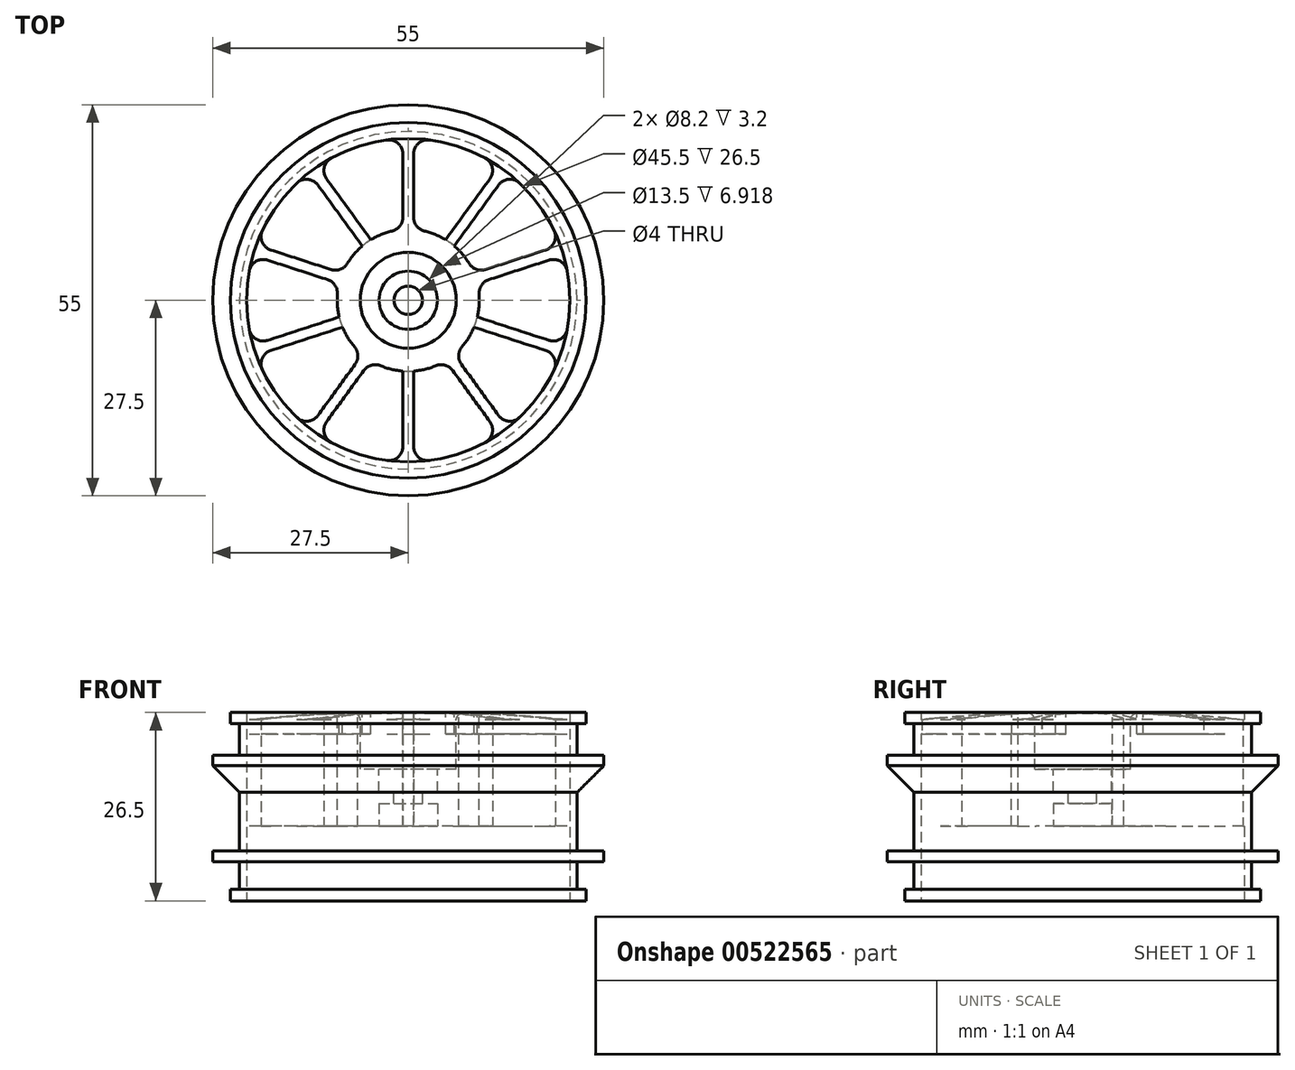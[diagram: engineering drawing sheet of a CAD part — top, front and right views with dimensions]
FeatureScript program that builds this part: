
annotation { "Feature Type Name" : "Feature", "Feature Type Description" : "" }
export const myFeature = defineFeature(function(context is Context, id is Id, definition is map)
    precondition{}
    {
        {
            var Q0;
            Q0=qCreatedBy(makeId("Top.planeOp"),FACE);
            var sketch = newSketch(context, id + "F0", { "sketchPlane" : qUnion([Q0])});
            skCircle(sketch, "E0", {"center": v(0, 0) * mm, "radius": 23.75 * mm});
            skCircle(sketch, "E1", {"center": v(0, 0) * mm, "radius": 22.75 * mm});
            skSolve(sketch);
        }
        {
            var Q0;
            Q0 = qSketchRegion(id + "F0", true);
            extrude(context, id + "F1", {"entities" : qUnion([Q0]), "depth" : 26.5 * mm, "offsetDistance" : 25 * mm});
        }
        {
            var Q0;
            Q0=qCreatedBy(makeId("Top.planeOp"),FACE);
            var sketch = newSketch(context, id + "F2", { "sketchPlane" : qUnion([Q0])});
            skCircle(sketch, "E2", {"center": v(0, 0) * mm, "radius": 25 * mm});
            skCircle(sketch, "E3", {"center": v(0, 0) * mm, "radius": 22.75 * mm});
            skSolve(sketch);
        }
        {
            var Q0;
            Q0 = qSketchRegion(id + "F2", true);
            extrude(context, id + "F3", {"entities" : qUnion([Q0]), "operationType" : NewBodyOperationType.ADD, "depth" : 1.6 * mm, "offsetDistance" : 25 * mm});
        }
        {
            var Q0;
            Q0=makeQuery(id+"F1.opExtrude","CAP_FACE",FACE,{"disambiguationData":[OSD([sQuery(id+"F0.wireOp",EDGE,"E0"),sQuery(id+"F0.wireOp",EDGE,"E1")])],"isStart":false});
            var sketch = newSketch(context, id + "F4", { "sketchPlane" : qUnion([Q0])});
            skCircle(sketch, "E4", {"center": v(0, 0) * mm, "radius": 22.75 * mm});
            skCircle(sketch, "E5", {"center": v(0, 0) * mm, "radius": 25 * mm});
            skSolve(sketch);
        }
        {
            var Q0;
            Q0 = qSketchRegion(id + "F4", true);
            extrude(context, id + "F5", {"entities" : qUnion([Q0]), "operationType" : NewBodyOperationType.ADD, "oppositeDirection" : true, "depth" : 1.6 * mm, "offsetDistance" : 25 * mm});
        }
        {
            var Q0;
            Q0=qCreatedBy(makeId("Top.planeOp"),FACE);
            cPlane(context, id + "F6", {"entities" : qUnion([Q0]), "cplaneType" : CPlaneType.OFFSET, "offset" : 5.5 * mm, "width" : 150 * mm, "height" : 150 * mm});
        }
        {
            var Q0;
            Q0=qCreatedBy(id+"F6.planeOp",FACE);
            var sketch = newSketch(context, id + "F7", { "sketchPlane" : qUnion([Q0])});
            skCircle(sketch, "E6", {"center": v(0, 0) * mm, "radius": 27.5 * mm});
            skCircle(sketch, "E7", {"center": v(0, 0) * mm, "radius": 22.75 * mm});
            skSolve(sketch);
        }
        {
            var Q0;
            Q0 = qSketchRegion(id + "F7", true);
            extrude(context, id + "F8", {"entities" : qUnion([Q0]), "operationType" : NewBodyOperationType.ADD, "depth" : 1.5 * mm, "offsetDistance" : 25 * mm});
        }
        {
            var Q0;
            Q0=qCreatedBy(makeId("Top.planeOp"),FACE);
            cPlane(context, id + "F9", {"entities" : qUnion([Q0]), "cplaneType" : CPlaneType.OFFSET, "offset" : 19 * mm, "width" : 150 * mm, "height" : 150 * mm});
        }
        {
            var Q0;
            Q0=qCreatedBy(id+"F9.planeOp",FACE);
            var sketch = newSketch(context, id + "F10", { "sketchPlane" : qUnion([Q0])});
            skCircle(sketch, "E8", {"center": v(0, 0) * mm, "radius": 27.5 * mm});
            skCircle(sketch, "E9", {"center": v(0, 0) * mm, "radius": 22.75 * mm});
            skSolve(sketch);
        }
        {
            var Q0;
            Q0 = qSketchRegion(id + "F10", true);
            extrude(context, id + "F11", {"entities" : qUnion([Q0]), "operationType" : NewBodyOperationType.ADD, "depth" : 1.5 * mm, "offsetDistance" : 25 * mm});
        }
        {
            var Q0;
            Q0=makeQuery(id+"F5.boolean.opBoolean","MERGE",FACE,{"derivedFrom":[makeQuery(id+"F1.opExtrude","CAP_FACE",FACE,{"disambiguationData":[OSD([sQuery(id+"F0.wireOp",EDGE,"E0"),sQuery(id+"F0.wireOp",EDGE,"E1")])],"isStart":false}),makeQuery(id+"F5.opExtrude","CAP_FACE",FACE,{"disambiguationData":[OSD([sQuery(id+"F4.wireOp",EDGE,"E4"),sQuery(id+"F4.wireOp",EDGE,"E5")])],"isStart":true})]});
            var sketch = newSketch(context, id + "F12", { "sketchPlane" : qUnion([Q0])});
            skLineSegment(sketch, "E10.top", {"start": v(-0.75, 23) * mm, "end": v(0.75, 23) * mm});
            skLineSegment(sketch, "E10.left", {"start": v(-0.75, 9.97) * mm, "end": v(-0.75, 23) * mm});
            skLineSegment(sketch, "E10.right", {"start": v(0.75, 9.97) * mm, "end": v(0.75, 23) * mm});
            skArc(sketch, "E11", {"start": v(-0.75, 9.97) * mm, "mid": v(-5.88, 8.1) * mm, "end": v(-9.25, 3.8) * mm});
            skLineSegment(sketch, "E12.1.0", {"start": v(9.25, 3.8) * mm, "end": v(21.64, 7.82) * mm});
            skLineSegment(sketch, "E12.1.1", {"start": v(9.72, 2.37) * mm, "end": v(22.1, 6.4) * mm});
            skLineSegment(sketch, "E12.1.2", {"start": v(21.64, 7.82) * mm, "end": v(22.1, 6.4) * mm});
            skLineSegment(sketch, "E12.2.0", {"start": v(6.47, -7.63) * mm, "end": v(14.13, -18.17) * mm});
            skLineSegment(sketch, "E12.2.1", {"start": v(5.25, -8.5) * mm, "end": v(12.91, -19.05) * mm});
            skLineSegment(sketch, "E12.2.2", {"start": v(14.13, -18.17) * mm, "end": v(12.91, -19.05) * mm});
            skLineSegment(sketch, "E12.3.0", {"start": v(-5.25, -8.5) * mm, "end": v(-12.91, -19.05) * mm});
            skLineSegment(sketch, "E12.3.1", {"start": v(-6.47, -7.63) * mm, "end": v(-14.13, -18.17) * mm});
            skLineSegment(sketch, "E12.3.2", {"start": v(-12.91, -19.05) * mm, "end": v(-14.13, -18.17) * mm});
            skLineSegment(sketch, "E12.4.0", {"start": v(-9.72, 2.37) * mm, "end": v(-22.1, 6.4) * mm});
            skLineSegment(sketch, "E12.4.1", {"start": v(-9.25, 3.8) * mm, "end": v(-21.64, 7.82) * mm});
            skLineSegment(sketch, "E12.4.2", {"start": v(-22.1, 6.4) * mm, "end": v(-21.64, 7.82) * mm});
            skLineSegment(sketch, "E12.anchor1", {"start": v(0, 0) * mm, "end": v(-0.75, 9.97) * mm, "construction": true});
            skLineSegment(sketch, "E12.anchor2", {"start": v(0, 0) * mm, "end": v(-9.72, 2.37) * mm, "construction": true});
            skArc(sketch, "E13.trimOffspring", {"start": v(-9.72, 2.37) * mm, "mid": v(-9.51, -3.1) * mm, "end": v(-6.47, -7.63) * mm});
            skArc(sketch, "E14.trimOffspring", {"start": v(-5.25, -8.5) * mm, "mid": v(0, -10) * mm, "end": v(5.25, -8.5) * mm});
            skArc(sketch, "E15.trimOffspring", {"start": v(6.47, -7.63) * mm, "mid": v(9.51, -3.1) * mm, "end": v(9.72, 2.37) * mm});
            skArc(sketch, "E16.trimOffspring", {"start": v(9.25, 3.8) * mm, "mid": v(5.88, 8.1) * mm, "end": v(0.75, 9.97) * mm});
            skSolve(sketch);
        }
        {
            var Q0;
            Q0 = qSketchRegion(id + "F12", true);
            extrude(context, id + "F13", {"entities" : qUnion([Q0]), "operationType" : NewBodyOperationType.ADD, "oppositeDirection" : true, "depth" : 16 * mm, "offsetDistance" : 25 * mm});
        }
        {
            var Q0;
            Q0=makeQuery(id+"F11.boolean.opBoolean","INTERSECT",EDGE,{"derivedFrom":[makeQuery(id+"F8.boolean.opBoolean","SPLIT",FACE,{"disambiguationData":[TD([makeQuery(id+"F5.opExtrude","CAP_FACE",FACE,{"disambiguationData":[OSD([sQuery(id+"F4.wireOp",EDGE,"E4"),sQuery(id+"F4.wireOp",EDGE,"E5")])],"isStart":false})])],"derivedFrom":makeQuery(id+"F1.opExtrude","SWEPT_FACE",FACE,{"disambiguationData":[OSD([sQuery(id+"F0.wireOp",EDGE,"E0")])]})}),makeQuery(id+"F11.opExtrude","CAP_FACE",FACE,{"disambiguationData":[OSD([sQuery(id+"F10.wireOp",EDGE,"E8"),sQuery(id+"F10.wireOp",EDGE,"E9")])],"isStart":true})]});
            chamfer(context, id + "F14", {"entities" : qUnion([Q0]), "width" : 3.75 * mm, "tangentPropagation" : true});
        }
        {
            var Q0;
            Q0=makeQuery(id+"F13.boolean.opBoolean","MERGE",FACE,{"derivedFrom":[makeQuery(id+"F5.boolean.opBoolean","MERGE",FACE,{"derivedFrom":[makeQuery(id+"F1.opExtrude","CAP_FACE",FACE,{"disambiguationData":[OSD([sQuery(id+"F0.wireOp",EDGE,"E0"),sQuery(id+"F0.wireOp",EDGE,"E1")])],"isStart":false}),makeQuery(id+"F5.opExtrude","CAP_FACE",FACE,{"disambiguationData":[OSD([sQuery(id+"F4.wireOp",EDGE,"E4"),sQuery(id+"F4.wireOp",EDGE,"E5")])],"isStart":true})]}),makeQuery(id+"F13.opExtrude","CAP_FACE",FACE,{"disambiguationData":[OSD([sQuery(id+"F12.wireOp",EDGE,"E10.top"),sQuery(id+"F12.wireOp",EDGE,"E10.left"),sQuery(id+"F12.wireOp",EDGE,"E10.right"),sQuery(id+"F12.wireOp",EDGE,"E11"),sQuery(id+"F12.wireOp",EDGE,"E12.1.0"),sQuery(id+"F12.wireOp",EDGE,"E12.1.1"),sQuery(id+"F12.wireOp",EDGE,"E12.1.2"),sQuery(id+"F12.wireOp",EDGE,"E12.2.0"),sQuery(id+"F12.wireOp",EDGE,"E12.2.1"),sQuery(id+"F12.wireOp",EDGE,"E12.2.2"),sQuery(id+"F12.wireOp",EDGE,"E12.3.0"),sQuery(id+"F12.wireOp",EDGE,"E12.3.1"),sQuery(id+"F12.wireOp",EDGE,"E12.3.2"),sQuery(id+"F12.wireOp",EDGE,"E12.4.0"),sQuery(id+"F12.wireOp",EDGE,"E12.4.1"),sQuery(id+"F12.wireOp",EDGE,"E12.4.2"),sQuery(id+"F12.wireOp",EDGE,"E13.trimOffspring"),sQuery(id+"F12.wireOp",EDGE,"E14.trimOffspring"),sQuery(id+"F12.wireOp",EDGE,"E15.trimOffspring"),sQuery(id+"F12.wireOp",EDGE,"E16.trimOffspring")])],"isStart":true})]});
            var sketch = newSketch(context, id + "F15", { "sketchPlane" : qUnion([Q0])});
            skArc(sketch, "E17", {"start": v(-0.75, 9.97) * mm, "mid": v(-3.1, 9.51) * mm, "end": v(-5.25, 8.5) * mm});
            skLineSegment(sketch, "E18", {"start": v(-0.75, 9.97) * mm, "end": v(-0.75, 22.97) * mm});
            skLineSegment(sketch, "E19", {"start": v(0.75, 22.97) * mm, "end": v(0.75, 9.97) * mm});
            skLineSegment(sketch, "E20.1.0", {"start": v(-6.47, 7.63) * mm, "end": v(-14.11, 18.14) * mm});
            skLineSegment(sketch, "E20.1.1", {"start": v(-12.9, 19.02) * mm, "end": v(-5.25, 8.5) * mm});
            skLineSegment(sketch, "E20.2.0", {"start": v(-9.72, 2.37) * mm, "end": v(-22.08, 6.38) * mm});
            skLineSegment(sketch, "E20.2.1", {"start": v(-21.62, 7.8) * mm, "end": v(-9.25, 3.8) * mm});
            skLineSegment(sketch, "E20.3.0", {"start": v(-9.25, -3.8) * mm, "end": v(-21.62, -7.81) * mm});
            skLineSegment(sketch, "E20.3.1", {"start": v(-22.08, -6.39) * mm, "end": v(-9.72, -2.37) * mm});
            skLineSegment(sketch, "E20.4.0", {"start": v(-5.25, -8.5) * mm, "end": v(-12.9, -19.03) * mm});
            skLineSegment(sketch, "E20.4.1", {"start": v(-14.1, -18.15) * mm, "end": v(-6.47, -7.63) * mm});
            skLineSegment(sketch, "E20.5.0", {"start": v(0.75, -9.97) * mm, "end": v(0.75, -22.97) * mm});
            skLineSegment(sketch, "E20.5.1", {"start": v(-0.75, -22.97) * mm, "end": v(-0.75, -9.97) * mm});
            skLineSegment(sketch, "E20.6.0", {"start": v(6.47, -7.63) * mm, "end": v(14.11, -18.14) * mm});
            skLineSegment(sketch, "E20.6.1", {"start": v(12.9, -19.02) * mm, "end": v(5.25, -8.5) * mm});
            skLineSegment(sketch, "E20.7.0", {"start": v(9.72, -2.37) * mm, "end": v(22.08, -6.38) * mm});
            skLineSegment(sketch, "E20.7.1", {"start": v(21.62, -7.8) * mm, "end": v(9.25, -3.8) * mm});
            skLineSegment(sketch, "E20.8.0", {"start": v(9.25, 3.8) * mm, "end": v(21.62, 7.81) * mm});
            skLineSegment(sketch, "E20.8.1", {"start": v(22.08, 6.39) * mm, "end": v(9.72, 2.37) * mm});
            skLineSegment(sketch, "E20.9.0", {"start": v(5.25, 8.5) * mm, "end": v(12.9, 19.03) * mm});
            skLineSegment(sketch, "E20.9.1", {"start": v(14.1, 18.15) * mm, "end": v(6.47, 7.63) * mm});
            skArc(sketch, "E21.trimOffspring", {"start": v(-9.72, 2.37) * mm, "mid": v(-10, 0) * mm, "end": v(-9.72, -2.37) * mm});
            skArc(sketch, "E22.trimOffspring", {"start": v(-5.25, -8.5) * mm, "mid": v(-3.1, -9.51) * mm, "end": v(-0.75, -9.97) * mm});
            skArc(sketch, "E23.trimOffspring", {"start": v(9.72, -2.37) * mm, "mid": v(10, 0) * mm, "end": v(9.72, 2.37) * mm});
            skArc(sketch, "E24.trimOffspring", {"start": v(6.47, -7.63) * mm, "mid": v(8.1, -5.88) * mm, "end": v(9.25, -3.8) * mm});
            skArc(sketch, "E25.trimOffspring", {"start": v(0.75, -9.97) * mm, "mid": v(3.1, -9.51) * mm, "end": v(5.25, -8.5) * mm});
            skArc(sketch, "E26.trimOffspring", {"start": v(-9.25, -3.8) * mm, "mid": v(-8.1, -5.88) * mm, "end": v(-6.47, -7.63) * mm});
            skArc(sketch, "E27.trimOffspring", {"start": v(-6.47, 7.63) * mm, "mid": v(-8.1, 5.88) * mm, "end": v(-9.25, 3.8) * mm});
            skArc(sketch, "E28.trimOffspring", {"start": v(5.25, 8.5) * mm, "mid": v(3.1, 9.51) * mm, "end": v(0.75, 9.97) * mm});
            skArc(sketch, "E29.trimOffspring", {"start": v(9.25, 3.8) * mm, "mid": v(8.1, 5.88) * mm, "end": v(6.47, 7.63) * mm});
            skLineSegment(sketch, "E30", {"start": v(-12.9, 19.02) * mm, "end": v(-14.11, 18.14) * mm});
            skLineSegment(sketch, "E31", {"start": v(-21.62, 7.8) * mm, "end": v(-22.08, 6.38) * mm});
            skLineSegment(sketch, "E32", {"start": v(-22.08, -6.39) * mm, "end": v(-21.62, -7.81) * mm});
            skLineSegment(sketch, "E33", {"start": v(-14.1, -18.15) * mm, "end": v(-12.9, -19.03) * mm});
            skLineSegment(sketch, "E34", {"start": v(-0.75, -22.97) * mm, "end": v(0.75, -22.97) * mm});
            skLineSegment(sketch, "E35", {"start": v(14.11, -18.14) * mm, "end": v(12.9, -19.02) * mm});
            skLineSegment(sketch, "E36", {"start": v(22.08, -6.38) * mm, "end": v(21.62, -7.8) * mm});
            skLineSegment(sketch, "E37", {"start": v(21.62, 7.81) * mm, "end": v(22.08, 6.39) * mm});
            skLineSegment(sketch, "E38", {"start": v(12.9, 19.03) * mm, "end": v(14.1, 18.15) * mm});
            skLineSegment(sketch, "E39", {"start": v(-0.75, 22.97) * mm, "end": v(0.75, 22.97) * mm});
            skSolve(sketch);
        }
        {
            var Q0;
            Q0 = qSketchRegion(id + "F15", true);
            extrude(context, id + "F16", {"entities" : qUnion([Q0]), "operationType" : NewBodyOperationType.ADD, "oppositeDirection" : true, "depth" : 3 * mm, "offsetDistance" : 25 * mm});
        }
        {
            var Q0;
            Q0=makeQuery(id+"F16.boolean.opBoolean","INTERSECT",EDGE,{"derivedFrom":[makeQuery(id+"F1.opExtrude","SWEPT_FACE",FACE,{"disambiguationData":[OSD([sQuery(id+"F0.wireOp",EDGE,"E1")])]}),makeQuery(id+"F16.opExtrude","SWEPT_FACE",FACE,{"disambiguationData":[OSD([sQuery(id+"F15.wireOp",EDGE,"E20.1.0")])]})]});
            var Q1;
            Q1=makeQuery(id+"F16.boolean.opBoolean","INTERSECT",EDGE,{"derivedFrom":[makeQuery(id+"F1.opExtrude","SWEPT_FACE",FACE,{"disambiguationData":[OSD([sQuery(id+"F0.wireOp",EDGE,"E1")])]}),makeQuery(id+"F16.opExtrude","SWEPT_FACE",FACE,{"disambiguationData":[OSD([sQuery(id+"F15.wireOp",EDGE,"E20.1.1")])]})]});
            var Q2;
            Q2=makeQuery(id+"F16.opExtrude","SWEPT_EDGE",EDGE,{"disambiguationData":[OSD([sQuery(id+"F12.wireOp",EDGE,"E11"),sQuery(id+"F15.wireOp",EDGE,"E20.1.0"),sQuery(id+"F15.wireOp",EDGE,"E27.trimOffspring")])]});
            var Q3;
            Q3=makeQuery(id+"F13.boolean.opBoolean","INTERSECT",EDGE,{"derivedFrom":[makeQuery(id+"F1.opExtrude","SWEPT_FACE",FACE,{"disambiguationData":[OSD([sQuery(id+"F0.wireOp",EDGE,"E1")])]}),makeQuery(id+"F13.opExtrude","SWEPT_FACE",FACE,{"disambiguationData":[OSD([sQuery(id+"F12.wireOp",EDGE,"E12.4.1")])]})]});
            var Q4;
            Q4=makeQuery(id+"F13.opExtrude","SWEPT_EDGE",EDGE,{"disambiguationData":[OSD([sQuery(id+"F12.wireOp",EDGE,"E11"),sQuery(id+"F12.wireOp",EDGE,"E12.4.1")])]});
            var Q5;
            Q5=makeQuery(id+"F13.opExtrude","SWEPT_EDGE",EDGE,{"disambiguationData":[OSD([sQuery(id+"F12.wireOp",EDGE,"E10.left"),sQuery(id+"F12.wireOp",EDGE,"E11")])]});
            var Q6;
            Q6=makeQuery(id+"F13.boolean.opBoolean","INTERSECT",EDGE,{"derivedFrom":[makeQuery(id+"F1.opExtrude","SWEPT_FACE",FACE,{"disambiguationData":[OSD([sQuery(id+"F0.wireOp",EDGE,"E1")])]}),makeQuery(id+"F13.opExtrude","SWEPT_FACE",FACE,{"disambiguationData":[OSD([sQuery(id+"F12.wireOp",EDGE,"E10.left")])]})]});
            var Q7;
            Q7=makeQuery(id+"F16.opExtrude","SWEPT_EDGE",EDGE,{"disambiguationData":[OSD([sQuery(id+"F12.wireOp",EDGE,"E11"),sQuery(id+"F15.wireOp",EDGE,"E17"),sQuery(id+"F15.wireOp",EDGE,"E20.1.1")])]});
            var Q8;
            Q8=makeQuery(id+"F16.opExtrude","SWEPT_EDGE",EDGE,{"disambiguationData":[OSD([sQuery(id+"F12.wireOp",EDGE,"E16.trimOffspring"),sQuery(id+"F15.wireOp",EDGE,"E20.9.0"),sQuery(id+"F15.wireOp",EDGE,"E28.trimOffspring")])]});
            var Q9;
            Q9=makeQuery(id+"F13.opExtrude","SWEPT_EDGE",EDGE,{"disambiguationData":[OSD([sQuery(id+"F12.wireOp",EDGE,"E10.right"),sQuery(id+"F12.wireOp",EDGE,"E16.trimOffspring")])]});
            var Q10;
            Q10=makeQuery(id+"F13.opExtrude","SWEPT_EDGE",EDGE,{"disambiguationData":[OSD([sQuery(id+"F12.wireOp",EDGE,"E12.1.0"),sQuery(id+"F12.wireOp",EDGE,"E16.trimOffspring")])]});
            var Q11;
            Q11=makeQuery(id+"F13.boolean.opBoolean","INTERSECT",EDGE,{"derivedFrom":[makeQuery(id+"F1.opExtrude","SWEPT_FACE",FACE,{"disambiguationData":[OSD([sQuery(id+"F0.wireOp",EDGE,"E1")])]}),makeQuery(id+"F13.opExtrude","SWEPT_FACE",FACE,{"disambiguationData":[OSD([sQuery(id+"F12.wireOp",EDGE,"E10.right")])]})]});
            var Q12;
            Q12=makeQuery(id+"F16.boolean.opBoolean","INTERSECT",EDGE,{"derivedFrom":[makeQuery(id+"F1.opExtrude","SWEPT_FACE",FACE,{"disambiguationData":[OSD([sQuery(id+"F0.wireOp",EDGE,"E1")])]}),makeQuery(id+"F16.opExtrude","SWEPT_FACE",FACE,{"disambiguationData":[OSD([sQuery(id+"F15.wireOp",EDGE,"E20.9.0")])]})]});
            var Q13;
            Q13=makeQuery(id+"F13.boolean.opBoolean","INTERSECT",EDGE,{"derivedFrom":[makeQuery(id+"F1.opExtrude","SWEPT_FACE",FACE,{"disambiguationData":[OSD([sQuery(id+"F0.wireOp",EDGE,"E1")])]}),makeQuery(id+"F13.opExtrude","SWEPT_FACE",FACE,{"disambiguationData":[OSD([sQuery(id+"F12.wireOp",EDGE,"E12.1.0")])]})]});
            var Q14;
            Q14=makeQuery(id+"F13.boolean.opBoolean","INTERSECT",EDGE,{"derivedFrom":[makeQuery(id+"F1.opExtrude","SWEPT_FACE",FACE,{"disambiguationData":[OSD([sQuery(id+"F0.wireOp",EDGE,"E1")])]}),makeQuery(id+"F13.opExtrude","SWEPT_FACE",FACE,{"disambiguationData":[OSD([sQuery(id+"F12.wireOp",EDGE,"E12.1.1")])]})]});
            var Q15;
            Q15=makeQuery(id+"F13.opExtrude","SWEPT_EDGE",EDGE,{"disambiguationData":[OSD([sQuery(id+"F12.wireOp",EDGE,"E12.1.1"),sQuery(id+"F12.wireOp",EDGE,"E15.trimOffspring")])]});
            var Q16;
            Q16=makeQuery(id+"F16.opExtrude","SWEPT_EDGE",EDGE,{"disambiguationData":[OSD([sQuery(id+"F12.wireOp",EDGE,"E15.trimOffspring"),sQuery(id+"F15.wireOp",EDGE,"E20.7.1"),sQuery(id+"F15.wireOp",EDGE,"E24.trimOffspring")])]});
            var Q17;
            Q17=makeQuery(id+"F13.opExtrude","SWEPT_EDGE",EDGE,{"disambiguationData":[OSD([sQuery(id+"F12.wireOp",EDGE,"E12.2.0"),sQuery(id+"F12.wireOp",EDGE,"E15.trimOffspring")])]});
            var Q18;
            Q18=makeQuery(id+"F16.opExtrude","SWEPT_EDGE",EDGE,{"disambiguationData":[OSD([sQuery(id+"F12.wireOp",EDGE,"E14.trimOffspring"),sQuery(id+"F15.wireOp",EDGE,"E20.5.0"),sQuery(id+"F15.wireOp",EDGE,"E25.trimOffspring")])]});
            var Q19;
            Q19=makeQuery(id+"F13.boolean.opBoolean","INTERSECT",EDGE,{"derivedFrom":[makeQuery(id+"F1.opExtrude","SWEPT_FACE",FACE,{"disambiguationData":[OSD([sQuery(id+"F0.wireOp",EDGE,"E1")])]}),makeQuery(id+"F13.opExtrude","SWEPT_FACE",FACE,{"disambiguationData":[OSD([sQuery(id+"F12.wireOp",EDGE,"E12.3.0")])]})]});
            var Q20;
            Q20=makeQuery(id+"F16.boolean.opBoolean","INTERSECT",EDGE,{"derivedFrom":[makeQuery(id+"F1.opExtrude","SWEPT_FACE",FACE,{"disambiguationData":[OSD([sQuery(id+"F0.wireOp",EDGE,"E1")])]}),makeQuery(id+"F16.opExtrude","SWEPT_FACE",FACE,{"disambiguationData":[OSD([sQuery(id+"F15.wireOp",EDGE,"E20.3.0")])]})]});
            var Q21;
            Q21=makeQuery(id+"F13.boolean.opBoolean","INTERSECT",EDGE,{"derivedFrom":[makeQuery(id+"F1.opExtrude","SWEPT_FACE",FACE,{"disambiguationData":[OSD([sQuery(id+"F0.wireOp",EDGE,"E1")])]}),makeQuery(id+"F13.opExtrude","SWEPT_FACE",FACE,{"disambiguationData":[OSD([sQuery(id+"F12.wireOp",EDGE,"E12.4.0")])]})]});
            var Q22;
            Q22=makeQuery(id+"F16.boolean.opBoolean","INTERSECT",EDGE,{"derivedFrom":[makeQuery(id+"F1.opExtrude","SWEPT_FACE",FACE,{"disambiguationData":[OSD([sQuery(id+"F0.wireOp",EDGE,"E1")])]}),makeQuery(id+"F16.opExtrude","SWEPT_FACE",FACE,{"disambiguationData":[OSD([sQuery(id+"F15.wireOp",EDGE,"E20.9.1")])]})]});
            var Q23;
            Q23=makeQuery(id+"F16.boolean.opBoolean","INTERSECT",EDGE,{"derivedFrom":[makeQuery(id+"F1.opExtrude","SWEPT_FACE",FACE,{"disambiguationData":[OSD([sQuery(id+"F0.wireOp",EDGE,"E1")])]}),makeQuery(id+"F16.opExtrude","SWEPT_FACE",FACE,{"disambiguationData":[OSD([sQuery(id+"F15.wireOp",EDGE,"E20.7.1")])]})]});
            var Q24;
            Q24=makeQuery(id+"F16.opExtrude","SWEPT_EDGE",EDGE,{"disambiguationData":[OSD([sQuery(id+"F12.wireOp",EDGE,"E13.trimOffspring"),sQuery(id+"F15.wireOp",EDGE,"E20.3.0"),sQuery(id+"F15.wireOp",EDGE,"E26.trimOffspring")])]});
            var Q25;
            Q25=makeQuery(id+"F13.opExtrude","SWEPT_EDGE",EDGE,{"disambiguationData":[OSD([sQuery(id+"F12.wireOp",EDGE,"E12.4.0"),sQuery(id+"F12.wireOp",EDGE,"E13.trimOffspring")])]});
            var Q26;
            Q26=makeQuery(id+"F13.opExtrude","SWEPT_EDGE",EDGE,{"disambiguationData":[OSD([sQuery(id+"F12.wireOp",EDGE,"E12.3.1"),sQuery(id+"F12.wireOp",EDGE,"E13.trimOffspring")])]});
            var Q27;
            Q27=makeQuery(id+"F16.opExtrude","SWEPT_EDGE",EDGE,{"disambiguationData":[OSD([sQuery(id+"F12.wireOp",EDGE,"E14.trimOffspring"),sQuery(id+"F15.wireOp",EDGE,"E20.5.1"),sQuery(id+"F15.wireOp",EDGE,"E22.trimOffspring")])]});
            var Q28;
            Q28=makeQuery(id+"F13.opExtrude","SWEPT_EDGE",EDGE,{"disambiguationData":[OSD([sQuery(id+"F12.wireOp",EDGE,"E12.2.1"),sQuery(id+"F12.wireOp",EDGE,"E14.trimOffspring")])]});
            var Q29;
            Q29=makeQuery(id+"F13.boolean.opBoolean","INTERSECT",EDGE,{"derivedFrom":[makeQuery(id+"F1.opExtrude","SWEPT_FACE",FACE,{"disambiguationData":[OSD([sQuery(id+"F0.wireOp",EDGE,"E1")])]}),makeQuery(id+"F13.opExtrude","SWEPT_FACE",FACE,{"disambiguationData":[OSD([sQuery(id+"F12.wireOp",EDGE,"E12.2.1")])]})]});
            var Q30;
            Q30=makeQuery(id+"F13.boolean.opBoolean","INTERSECT",EDGE,{"derivedFrom":[makeQuery(id+"F1.opExtrude","SWEPT_FACE",FACE,{"disambiguationData":[OSD([sQuery(id+"F0.wireOp",EDGE,"E1")])]}),makeQuery(id+"F13.opExtrude","SWEPT_FACE",FACE,{"disambiguationData":[OSD([sQuery(id+"F12.wireOp",EDGE,"E12.2.0")])]})]});
            var Q31;
            Q31=makeQuery(id+"F16.boolean.opBoolean","INTERSECT",EDGE,{"derivedFrom":[makeQuery(id+"F1.opExtrude","SWEPT_FACE",FACE,{"disambiguationData":[OSD([sQuery(id+"F0.wireOp",EDGE,"E1")])]}),makeQuery(id+"F16.opExtrude","SWEPT_FACE",FACE,{"disambiguationData":[OSD([sQuery(id+"F15.wireOp",EDGE,"E20.5.0")])]})]});
            var Q32;
            Q32=makeQuery(id+"F16.boolean.opBoolean","INTERSECT",EDGE,{"derivedFrom":[makeQuery(id+"F1.opExtrude","SWEPT_FACE",FACE,{"disambiguationData":[OSD([sQuery(id+"F0.wireOp",EDGE,"E1")])]}),makeQuery(id+"F16.opExtrude","SWEPT_FACE",FACE,{"disambiguationData":[OSD([sQuery(id+"F15.wireOp",EDGE,"E20.5.1")])]})]});
            var Q33;
            Q33=makeQuery(id+"F13.boolean.opBoolean","INTERSECT",EDGE,{"derivedFrom":[makeQuery(id+"F1.opExtrude","SWEPT_FACE",FACE,{"disambiguationData":[OSD([sQuery(id+"F0.wireOp",EDGE,"E1")])]}),makeQuery(id+"F13.opExtrude","SWEPT_FACE",FACE,{"disambiguationData":[OSD([sQuery(id+"F12.wireOp",EDGE,"E12.3.1")])]})]});
            var Q34;
            Q34=makeQuery(id+"F16.boolean.opBoolean","INTERSECT",EDGE,{"derivedFrom":[makeQuery(id+"F1.opExtrude","SWEPT_FACE",FACE,{"disambiguationData":[OSD([sQuery(id+"F0.wireOp",EDGE,"E1")])]}),makeQuery(id+"F16.opExtrude","SWEPT_FACE",FACE,{"disambiguationData":[OSD([sQuery(id+"F15.wireOp",EDGE,"E20.3.1")])]})]});
            var Q35;
            Q35=makeQuery(id+"F13.opExtrude","SWEPT_EDGE",EDGE,{"disambiguationData":[OSD([sQuery(id+"F12.wireOp",EDGE,"E12.3.0"),sQuery(id+"F12.wireOp",EDGE,"E14.trimOffspring")])]});
            var Q36;
            Q36=makeQuery(id+"F16.opExtrude","SWEPT_EDGE",EDGE,{"disambiguationData":[OSD([sQuery(id+"F12.wireOp",EDGE,"E16.trimOffspring"),sQuery(id+"F15.wireOp",EDGE,"E20.9.1"),sQuery(id+"F15.wireOp",EDGE,"E29.trimOffspring")])]});
            var Q37;
            Q37=makeQuery(id+"F16.opExtrude","SWEPT_EDGE",EDGE,{"disambiguationData":[OSD([sQuery(id+"F12.wireOp",EDGE,"E15.trimOffspring"),sQuery(id+"F15.wireOp",EDGE,"E20.7.0"),sQuery(id+"F15.wireOp",EDGE,"E23.trimOffspring")])]});
            var Q38;
            Q38=makeQuery(id+"F16.boolean.opBoolean","INTERSECT",EDGE,{"derivedFrom":[makeQuery(id+"F1.opExtrude","SWEPT_FACE",FACE,{"disambiguationData":[OSD([sQuery(id+"F0.wireOp",EDGE,"E1")])]}),makeQuery(id+"F16.opExtrude","SWEPT_FACE",FACE,{"disambiguationData":[OSD([sQuery(id+"F15.wireOp",EDGE,"E20.7.0")])]})]});
            var Q39;
            Q39=makeQuery(id+"F16.opExtrude","SWEPT_EDGE",EDGE,{"disambiguationData":[OSD([sQuery(id+"F12.wireOp",EDGE,"E13.trimOffspring"),sQuery(id+"F15.wireOp",EDGE,"E20.3.1"),sQuery(id+"F15.wireOp",EDGE,"E21.trimOffspring")])]});
            fillet(context, id + "F17", {"entities" : qUnion([Q0, Q1, Q2, Q3, Q4, Q5, Q6, Q7, Q8, Q9, Q10, Q11, Q12, Q13, Q14, Q15, Q16, Q17, Q18, Q19, Q20, Q21, Q22, Q23, Q24, Q25, Q26, Q27, Q28, Q29, Q30, Q31, Q32, Q33, Q34, Q35, Q36, Q37, Q38, Q39]), "radius" : 2 * mm, "tangentPropagation" : true, "allowEdgeOverflow" : false});
        }
        {
            var Q0;
            Q0=qCreatedBy(makeId("Front.planeOp"),FACE);
            var sketch = newSketch(context, id + "F18", { "sketchPlane" : qUnion([Q0])});
            skLineSegment(sketch, "E40", {"start": v(0, 27.5) * mm, "end": v(22.75, 27.5) * mm});
            skLineSegment(sketch, "E41", {"start": v(22.75, 27.5) * mm, "end": v(22.75, 25.5) * mm});
            skFitSpline(sketch, "E42", {"points": [v(22.75, 25.5) * mm, v(12.74, 26.28) * mm, v(0, 26.5) * mm], "startDerivative": vector(-15.68, 1.36) * mm, "endDerivative": vector(-21.9, 0.46) * mm});
            skLineSegment(sketch, "E43", {"start": v(0, 26.5) * mm, "end": v(0, 27.5) * mm});
            skSolve(sketch);
        }
        {
            var Q0;
            Q0 = qSketchRegion(id + "F18", true);
            var Q1;
            Q1=sQuery(id+"F18.wireOp",EDGE,"E43");
            revolve(context, id + "F19", {"operationType" : NewBodyOperationType.REMOVE, "entities" : qUnion([Q0]), "axis" : qUnion([Q1]), "revolveType" : RevolveType.FULL});
        }
        {
            var Q0;
            Q0=makeQuery(id+"F16.boolean.opBoolean","MERGE",FACE,{"derivedFrom":[makeQuery(id+"F13.boolean.opBoolean","MERGE",FACE,{"derivedFrom":[makeQuery(id+"F5.boolean.opBoolean","MERGE",FACE,{"derivedFrom":[makeQuery(id+"F1.opExtrude","CAP_FACE",FACE,{"disambiguationData":[OSD([sQuery(id+"F0.wireOp",EDGE,"E0"),sQuery(id+"F0.wireOp",EDGE,"E1")])],"isStart":false}),makeQuery(id+"F5.opExtrude","CAP_FACE",FACE,{"disambiguationData":[OSD([sQuery(id+"F4.wireOp",EDGE,"E4"),sQuery(id+"F4.wireOp",EDGE,"E5")])],"isStart":true})]}),makeQuery(id+"F13.opExtrude","CAP_FACE",FACE,{"disambiguationData":[OSD([sQuery(id+"F12.wireOp",EDGE,"E10.top"),sQuery(id+"F12.wireOp",EDGE,"E10.left"),sQuery(id+"F12.wireOp",EDGE,"E10.right"),sQuery(id+"F12.wireOp",EDGE,"E11"),sQuery(id+"F12.wireOp",EDGE,"E12.1.0"),sQuery(id+"F12.wireOp",EDGE,"E12.1.1"),sQuery(id+"F12.wireOp",EDGE,"E12.1.2"),sQuery(id+"F12.wireOp",EDGE,"E12.2.0"),sQuery(id+"F12.wireOp",EDGE,"E12.2.1"),sQuery(id+"F12.wireOp",EDGE,"E12.2.2"),sQuery(id+"F12.wireOp",EDGE,"E12.3.0"),sQuery(id+"F12.wireOp",EDGE,"E12.3.1"),sQuery(id+"F12.wireOp",EDGE,"E12.3.2"),sQuery(id+"F12.wireOp",EDGE,"E12.4.0"),sQuery(id+"F12.wireOp",EDGE,"E12.4.1"),sQuery(id+"F12.wireOp",EDGE,"E12.4.2"),sQuery(id+"F12.wireOp",EDGE,"E13.trimOffspring"),sQuery(id+"F12.wireOp",EDGE,"E14.trimOffspring"),sQuery(id+"F12.wireOp",EDGE,"E15.trimOffspring"),sQuery(id+"F12.wireOp",EDGE,"E16.trimOffspring")])],"isStart":true})]}),makeQuery(id+"F16.opExtrude","CAP_FACE",FACE,{"disambiguationData":[OSD([sQuery(id+"F15.wireOp",EDGE,"E17"),sQuery(id+"F15.wireOp",EDGE,"E18"),sQuery(id+"F15.wireOp",EDGE,"E19"),sQuery(id+"F15.wireOp",EDGE,"E20.1.0"),sQuery(id+"F15.wireOp",EDGE,"E20.1.1"),sQuery(id+"F15.wireOp",EDGE,"E20.2.0"),sQuery(id+"F15.wireOp",EDGE,"E20.2.1"),sQuery(id+"F15.wireOp",EDGE,"E20.3.0"),sQuery(id+"F15.wireOp",EDGE,"E20.3.1"),sQuery(id+"F15.wireOp",EDGE,"E20.4.0"),sQuery(id+"F15.wireOp",EDGE,"E20.4.1"),sQuery(id+"F15.wireOp",EDGE,"E20.5.0"),sQuery(id+"F15.wireOp",EDGE,"E20.5.1"),sQuery(id+"F15.wireOp",EDGE,"E20.6.0"),sQuery(id+"F15.wireOp",EDGE,"E20.6.1"),sQuery(id+"F15.wireOp",EDGE,"E20.7.0"),sQuery(id+"F15.wireOp",EDGE,"E20.7.1"),sQuery(id+"F15.wireOp",EDGE,"E20.8.0"),sQuery(id+"F15.wireOp",EDGE,"E20.8.1"),sQuery(id+"F15.wireOp",EDGE,"E20.9.0"),sQuery(id+"F15.wireOp",EDGE,"E20.9.1"),sQuery(id+"F15.wireOp",EDGE,"E21.trimOffspring"),sQuery(id+"F15.wireOp",EDGE,"E22.trimOffspring"),sQuery(id+"F15.wireOp",EDGE,"E23.trimOffspring"),sQuery(id+"F15.wireOp",EDGE,"E24.trimOffspring"),sQuery(id+"F15.wireOp",EDGE,"E25.trimOffspring"),sQuery(id+"F15.wireOp",EDGE,"E26.trimOffspring"),sQuery(id+"F15.wireOp",EDGE,"E27.trimOffspring"),sQuery(id+"F15.wireOp",EDGE,"E28.trimOffspring"),sQuery(id+"F15.wireOp",EDGE,"E29.trimOffspring"),sQuery(id+"F15.wireOp",EDGE,"E30"),sQuery(id+"F15.wireOp",EDGE,"E31"),sQuery(id+"F15.wireOp",EDGE,"E32"),sQuery(id+"F15.wireOp",EDGE,"E33"),sQuery(id+"F15.wireOp",EDGE,"E34"),sQuery(id+"F15.wireOp",EDGE,"E35"),sQuery(id+"F15.wireOp",EDGE,"E36"),sQuery(id+"F15.wireOp",EDGE,"E37"),sQuery(id+"F15.wireOp",EDGE,"E38"),sQuery(id+"F15.wireOp",EDGE,"E39")])],"isStart":true})]});
            var sketch = newSketch(context, id + "F20", { "sketchPlane" : qUnion([Q0])});
            skCircle(sketch, "E44", {"center": v(0, 0) * mm, "radius": 6.75 * mm});
            skSolve(sketch);
        }
        {
            var Q0;
            Q0 = qSketchRegion(id + "F20", true);
            extrude(context, id + "F21", {"entities" : qUnion([Q0]), "operationType" : NewBodyOperationType.REMOVE, "oppositeDirection" : true, "depth" : 8 * mm, "offsetDistance" : 25 * mm});
        }
        {
            var Q0;
            Q0=makeQuery(id+"F21.boolean.opBoolean","INTERSECT",EDGE,{"derivedFrom":[makeQuery(id+"F19.boolean.opBoolean","COPY",FACE,{"derivedFrom":makeQuery(id+"F19.opRevolve","SWEPT_FACE",FACE,{"disambiguationData":[OSD([sQuery(id+"F18.wireOp",EDGE,"E42")])]})}),makeQuery(id+"F21.opExtrude","SWEPT_FACE",FACE,{"disambiguationData":[OSD([sQuery(id+"F20.wireOp",EDGE,"E44")])]})]});
            fillet(context, id + "F22", {"entities" : qUnion([Q0]), "radius" : 1 * mm, "tangentPropagation" : true, "allowEdgeOverflow" : false});
        }
        {
            var Q0;
            Q0=makeQuery(id+"F21.boolean.opBoolean","COPY",FACE,{"derivedFrom":makeQuery(id+"F21.opExtrude","CAP_FACE",FACE,{"disambiguationData":[OSD([sQuery(id+"F20.wireOp",EDGE,"E44")])],"isStart":false})});
            var sketch = newSketch(context, id + "F23", { "sketchPlane" : qUnion([Q0])});
            skCircle(sketch, "E45", {"center": v(0, 0) * mm, "radius": 4.1 * mm});
            skSolve(sketch);
        }
        {
            var Q0;
            Q0 = qSketchRegion(id + "F23", true);
            extrude(context, id + "F24", {"entities" : qUnion([Q0]), "operationType" : NewBodyOperationType.REMOVE, "oppositeDirection" : true, "depth" : 3.2 * mm, "offsetDistance" : 25 * mm});
        }
        {
            var Q0;
            Q0=makeQuery(id+"F13.opExtrude","CAP_FACE",FACE,{"disambiguationData":[OSD([sQuery(id+"F12.wireOp",EDGE,"E10.top"),sQuery(id+"F12.wireOp",EDGE,"E10.left"),sQuery(id+"F12.wireOp",EDGE,"E10.right"),sQuery(id+"F12.wireOp",EDGE,"E11"),sQuery(id+"F12.wireOp",EDGE,"E12.1.0"),sQuery(id+"F12.wireOp",EDGE,"E12.1.1"),sQuery(id+"F12.wireOp",EDGE,"E12.1.2"),sQuery(id+"F12.wireOp",EDGE,"E12.2.0"),sQuery(id+"F12.wireOp",EDGE,"E12.2.1"),sQuery(id+"F12.wireOp",EDGE,"E12.2.2"),sQuery(id+"F12.wireOp",EDGE,"E12.3.0"),sQuery(id+"F12.wireOp",EDGE,"E12.3.1"),sQuery(id+"F12.wireOp",EDGE,"E12.3.2"),sQuery(id+"F12.wireOp",EDGE,"E12.4.0"),sQuery(id+"F12.wireOp",EDGE,"E12.4.1"),sQuery(id+"F12.wireOp",EDGE,"E12.4.2"),sQuery(id+"F12.wireOp",EDGE,"E13.trimOffspring"),sQuery(id+"F12.wireOp",EDGE,"E14.trimOffspring"),sQuery(id+"F12.wireOp",EDGE,"E15.trimOffspring"),sQuery(id+"F12.wireOp",EDGE,"E16.trimOffspring")])],"isStart":false});
            var sketch = newSketch(context, id + "F25", { "sketchPlane" : qUnion([Q0])});
            skCircle(sketch, "E46", {"center": v(0, 0) * mm, "radius": 4.1 * mm});
            skSolve(sketch);
        }
        {
            var Q0;
            Q0 = qSketchRegion(id + "F25", true);
            extrude(context, id + "F26", {"entities" : qUnion([Q0]), "operationType" : NewBodyOperationType.REMOVE, "oppositeDirection" : true, "depth" : 3.2 * mm, "offsetDistance" : 25 * mm});
        }
        {
            var Q0;
            Q0=makeQuery(id+"F24.boolean.opBoolean","COPY",FACE,{"derivedFrom":makeQuery(id+"F24.opExtrude","CAP_FACE",FACE,{"disambiguationData":[OSD([sQuery(id+"F23.wireOp",EDGE,"E45")])],"isStart":false})});
            var sketch = newSketch(context, id + "F27", { "sketchPlane" : qUnion([Q0])});
            skCircle(sketch, "E47", {"center": v(0, 0) * mm, "radius": 2 * mm});
            skSolve(sketch);
        }
        {
            var Q0;
            Q0 = qSketchRegion(id + "F27", true);
            extrude(context, id + "F28", {"entities" : qUnion([Q0]), "operationType" : NewBodyOperationType.REMOVE, "oppositeDirection" : true, "depth" : 25 * mm, "offsetDistance" : 25 * mm});
        }
    });
